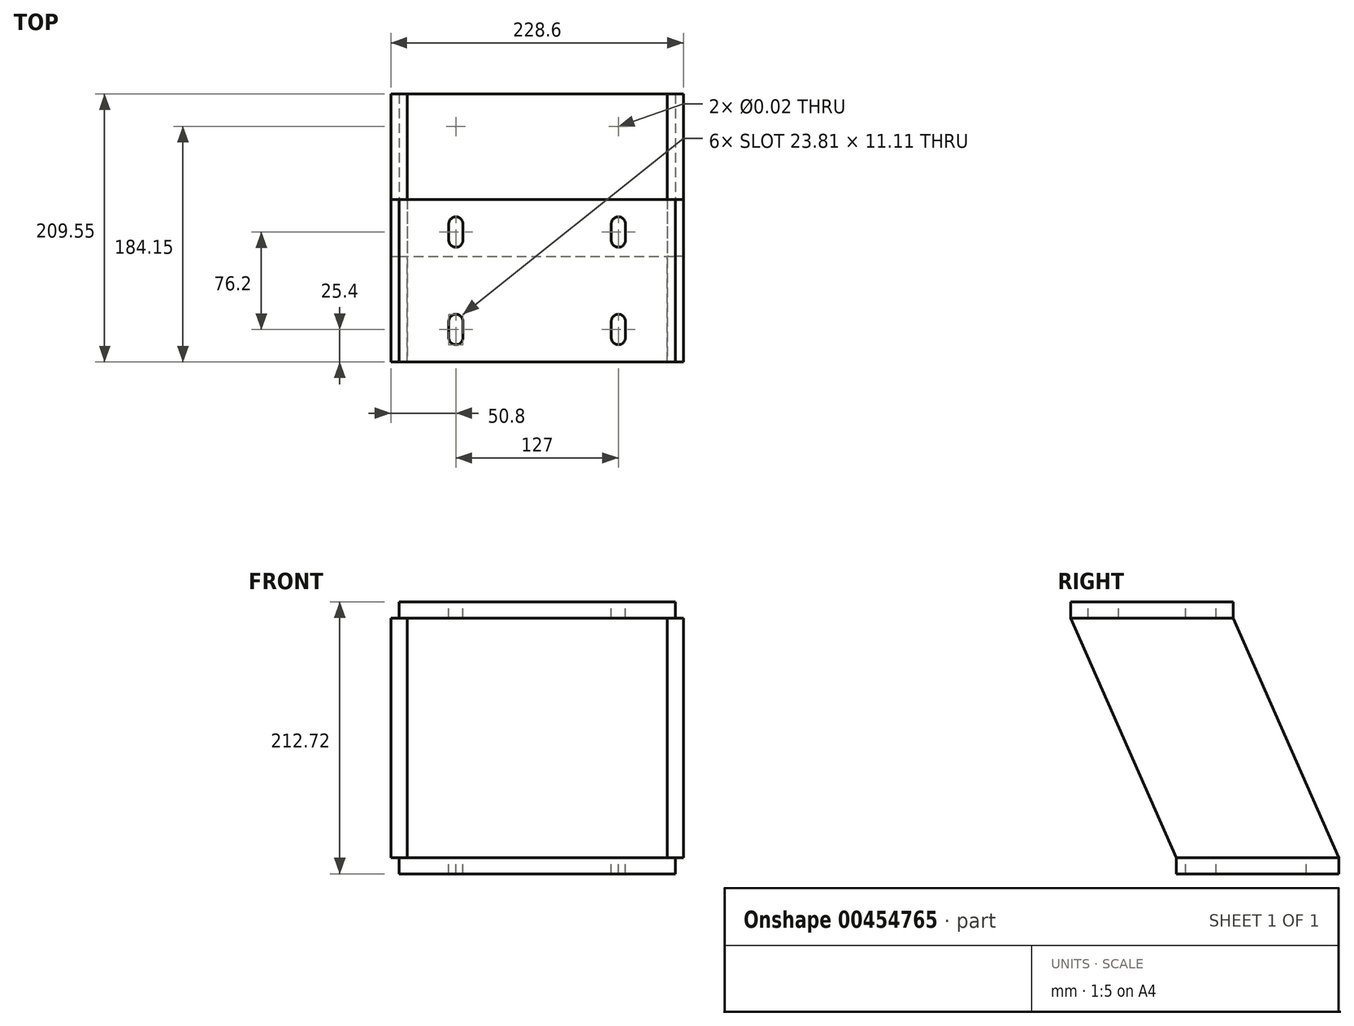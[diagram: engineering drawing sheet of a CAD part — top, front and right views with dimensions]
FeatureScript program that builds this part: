
annotation { "Feature Type Name" : "Feature", "Feature Type Description" : "" }
export const myFeature = defineFeature(function(context is Context, id is Id, definition is map)
    precondition{}
    {
        {
            var Q0;
            Q0=qCreatedBy(makeId("Top.planeOp"),FACE);
            var sketch = newSketch(context, id + "F0", { "sketchPlane" : qUnion([Q0])});
            skLineSegment(sketch, "E0.bottom", {"start": v(-107.95, 63.5) * mm, "end": v(107.95, 63.5) * mm});
            skLineSegment(sketch, "E0.top", {"start": v(-107.95, -63.5) * mm, "end": v(107.95, -63.5) * mm});
            skLineSegment(sketch, "E0.left", {"start": v(-107.95, 63.5) * mm, "end": v(-107.95, -63.5) * mm});
            skLineSegment(sketch, "E0.right", {"start": v(107.95, 63.5) * mm, "end": v(107.95, -63.5) * mm});
            skPoint(sketch, "E0.middle", {"position": v(0, 0) * mm});
            skSolve(sketch);
        }
        {
            var Q0;
            Q0=qSketchRegion(id+"F0",true);
            extrude(context, id + "F1", {"entities" : qUnion([Q0]), "depth" : 12.7 * mm});
        }
        {
            var Q0;
            Q0=makeQuery(id+"F1.opExtrude","CAP_FACE",FACE,{"disambiguationData":[OSD([sQuery(id+"F0.wireOp",EDGE,"E0.bottom"),sQuery(id+"F0.wireOp",EDGE,"E0.top"),sQuery(id+"F0.wireOp",EDGE,"E0.left"),sQuery(id+"F0.wireOp",EDGE,"E0.right")])],"isStart":false});
            var sketch = newSketch(context, id + "F2", { "sketchPlane" : qUnion([Q0])});
            skLineSegment(sketch, "E1.bottom", {"start": v(-63.5, 38.1) * mm, "end": v(63.5, 38.1) * mm, "construction": true});
            skLineSegment(sketch, "E1.top", {"start": v(-63.5, -38.1) * mm, "end": v(63.5, -38.1) * mm, "construction": true});
            skLineSegment(sketch, "E1.left", {"start": v(-63.5, 38.1) * mm, "end": v(-63.5, -38.1) * mm, "construction": true});
            skLineSegment(sketch, "E1.right", {"start": v(63.5, 38.1) * mm, "end": v(63.5, -38.1) * mm, "construction": true});
            skPoint(sketch, "E1.middle", {"position": v(0, 0) * mm});
            skPoint(sketch, "E2", {"position": v(-63.5, 38.1) * mm});
            skPoint(sketch, "E3", {"position": v(63.5, 38.1) * mm});
            skPoint(sketch, "E4", {"position": v(63.5, -38.1) * mm});
            skPoint(sketch, "E5", {"position": v(-63.5, -38.1) * mm});
            skSolve(sketch);
        }
        {
            var Q0;
            Q0=sQuery(id+"F2.wireOp",VERTEX,"E2");
            var Q1;
            Q1=sQuery(id+"F2.wireOp",VERTEX,"E3");
            var Q2;
            Q2=sQuery(id+"F2.wireOp",VERTEX,"E4");
            var Q3;
            Q3=sQuery(id+"F2.wireOp",VERTEX,"E5");
            var Q4;
            Q4=makeQuery(id+"F1.opExtrude","SWEPT_BODY",BODY,{"disambiguationData":[OSD([sQuery(id+"F0.wireOp",EDGE,"E0.bottom"),sQuery(id+"F0.wireOp",EDGE,"E0.top"),sQuery(id+"F0.wireOp",EDGE,"E0.left"),sQuery(id+"F0.wireOp",EDGE,"E0.right")])]});
            hole(context, id + "F3", {"style" : HoleStyle.SIMPLE, "endStyle" : HoleEndStyle.THROUGH, "standardTappedOrClearance" : lookupTablePath({ "standard" : "ANSI", "size" : "9/16 (0.56)", "type" : "Drilled" }), "standardBlindInLast" : lookupTablePath({ "standard" : "ANSI", "size" : "9/16", "type" : "Drilled" }), "holeDiameter" : 9 / 406.4 * mm, "locations" : qUnion([Q0, Q1, Q2, Q3]), "scope" : qUnion([Q4]), "isTappedThrough" : true});
        }
        {
            var Q0;
            Q0=qCreatedBy(makeId("Top.planeOp"),FACE);
            cPlane(context, id + "F4", {"entities" : qUnion([Q0]), "cplaneType" : CPlaneType.OFFSET, "offset" : 212.72 * mm, "width" : 152.4 * mm, "height" : 152.4 * mm});
        }
        {
            var Q0;
            Q0=qCreatedBy(id+"F4.planeOp",FACE);
            var sketch = newSketch(context, id + "F5", { "sketchPlane" : qUnion([Q0])});
            skLineSegment(sketch, "E6.0", {"start": v(-107.95, 63.5) * mm, "end": v(107.95, 63.5) * mm, "construction": true});
            skLineSegment(sketch, "E7.0", {"start": v(-107.95, -19.05) * mm, "end": v(107.95, -19.05) * mm, "construction": true});
            skLineSegment(sketch, "E8.bottom", {"start": v(-107.95, -19.05) * mm, "end": v(107.95, -19.05) * mm});
            skLineSegment(sketch, "E8.top", {"start": v(-107.95, -146.05) * mm, "end": v(107.95, -146.05) * mm});
            skLineSegment(sketch, "E8.left", {"start": v(-107.95, -19.05) * mm, "end": v(-107.95, -146.05) * mm});
            skLineSegment(sketch, "E8.right", {"start": v(107.95, -19.05) * mm, "end": v(107.95, -146.05) * mm});
            skSolve(sketch);
        }
        {
            var Q0;
            Q0=qSketchRegion(id+"F5",true);
            extrude(context, id + "F6", {"entities" : qUnion([Q0]), "oppositeDirection" : true, "depth" : 12.7 * mm});
        }
        {
            var Q0;
            Q0=makeQuery(id+"F6.opExtrude","CAP_FACE",FACE,{"disambiguationData":[OSD([sQuery(id+"F5.wireOp",EDGE,"E8.bottom"),sQuery(id+"F5.wireOp",EDGE,"E8.top"),sQuery(id+"F5.wireOp",EDGE,"E8.left"),sQuery(id+"F5.wireOp",EDGE,"E8.right")])],"isStart":true});
            var sketch = newSketch(context, id + "F7", { "sketchPlane" : qUnion([Q0])});
            skPoint(sketch, "E9.0", {"position": v(-107.95, -63.5) * mm});
            skLineSegment(sketch, "E10.0", {"start": v(-107.95, -19.05) * mm, "end": v(-107.95, -146.05) * mm, "construction": true});
            skLineSegment(sketch, "E11.0", {"start": v(107.95, -19.05) * mm, "end": v(107.95, -146.05) * mm, "construction": true});
            skLineSegment(sketch, "E12", {"start": v(-107.95, -19.05) * mm, "end": v(107.95, -146.05) * mm, "construction": true});
            skLineSegment(sketch, "E13", {"start": v(107.95, -19.05) * mm, "end": v(-107.95, -146.05) * mm, "construction": true});
            skLineSegment(sketch, "E14.bottom", {"start": v(-63.5, -44.45) * mm, "end": v(63.5, -44.45) * mm, "construction": true});
            skLineSegment(sketch, "E14.top", {"start": v(-63.5, -120.65) * mm, "end": v(63.5, -120.65) * mm, "construction": true});
            skLineSegment(sketch, "E14.left", {"start": v(-63.5, -44.45) * mm, "end": v(-63.5, -120.65) * mm, "construction": true});
            skLineSegment(sketch, "E14.right", {"start": v(63.5, -44.45) * mm, "end": v(63.5, -120.65) * mm, "construction": true});
            skPoint(sketch, "E14.middle", {"position": v(0, -82.55) * mm});
            skPoint(sketch, "E15", {"position": v(-63.5, -44.45) * mm});
            skPoint(sketch, "E16", {"position": v(63.5, -44.45) * mm});
            skPoint(sketch, "E17", {"position": v(63.5, -120.65) * mm});
            skPoint(sketch, "E18", {"position": v(-63.5, -120.65) * mm});
            skLineSegment(sketch, "E19", {"start": v(-63.5, -38.1) * mm, "end": v(-63.5, -50.8) * mm});
            skArc(sketch, "E20.0.startCap", {"start": v(-69.06, -38.1) * mm, "mid": v(-63.5, -32.54) * mm, "end": v(-57.94, -38.1) * mm});
            skArc(sketch, "E20.0.endCap", {"start": v(-57.94, -50.8) * mm, "mid": v(-63.5, -56.36) * mm, "end": v(-69.06, -50.8) * mm});
            skLineSegment(sketch, "E20.0.left", {"start": v(-57.94, -38.1) * mm, "end": v(-57.94, -50.8) * mm});
            skLineSegment(sketch, "E20.0.right", {"start": v(-69.06, -38.1) * mm, "end": v(-69.06, -50.8) * mm});
            skLineSegment(sketch, "E21.0.1.1", {"start": v(-63.5, -114.3) * mm, "end": v(-63.5, -127) * mm});
            skArc(sketch, "E21.0.1.2", {"start": v(-69.06, -114.3) * mm, "mid": v(-63.5, -108.74) * mm, "end": v(-57.94, -114.3) * mm});
            skArc(sketch, "E21.0.1.3", {"start": v(-57.94, -127) * mm, "mid": v(-63.5, -132.56) * mm, "end": v(-69.06, -127) * mm});
            skLineSegment(sketch, "E21.0.1.4", {"start": v(-57.94, -114.3) * mm, "end": v(-57.94, -127) * mm});
            skLineSegment(sketch, "E21.0.1.5", {"start": v(-69.06, -114.3) * mm, "end": v(-69.06, -127) * mm});
            skLineSegment(sketch, "E21.1.0.1", {"start": v(63.5, -38.1) * mm, "end": v(63.5, -50.8) * mm});
            skArc(sketch, "E21.1.0.2", {"start": v(57.94, -38.1) * mm, "mid": v(63.5, -32.54) * mm, "end": v(69.06, -38.1) * mm});
            skArc(sketch, "E21.1.0.3", {"start": v(69.06, -50.8) * mm, "mid": v(63.5, -56.36) * mm, "end": v(57.94, -50.8) * mm});
            skLineSegment(sketch, "E21.1.0.4", {"start": v(69.06, -38.1) * mm, "end": v(69.06, -50.8) * mm});
            skLineSegment(sketch, "E21.1.0.5", {"start": v(57.94, -38.1) * mm, "end": v(57.94, -50.8) * mm});
            skLineSegment(sketch, "E21.1.1.1", {"start": v(63.5, -114.3) * mm, "end": v(63.5, -127) * mm});
            skArc(sketch, "E21.1.1.2", {"start": v(57.94, -114.3) * mm, "mid": v(63.5, -108.74) * mm, "end": v(69.06, -114.3) * mm});
            skArc(sketch, "E21.1.1.3", {"start": v(69.06, -127) * mm, "mid": v(63.5, -132.56) * mm, "end": v(57.94, -127) * mm});
            skLineSegment(sketch, "E21.1.1.4", {"start": v(69.06, -114.3) * mm, "end": v(69.06, -127) * mm});
            skLineSegment(sketch, "E21.1.1.5", {"start": v(57.94, -114.3) * mm, "end": v(57.94, -127) * mm});
            skLineSegment(sketch, "E21.direction1", {"start": v(-69.06, -50.8) * mm, "end": v(57.94, -50.8) * mm, "construction": true});
            skLineSegment(sketch, "E21.direction2", {"start": v(-69.06, -50.8) * mm, "end": v(-69.06, -127) * mm, "construction": true});
            skSolve(sketch);
        }
        {
            var Q0;
            Q0=qSketchRegion(id+"F7",true);
            extrude(context, id + "F8", {"entities" : qUnion([Q0]), "operationType" : NewBodyOperationType.REMOVE, "endBound" : BoundingType.THROUGH_ALL, "oppositeDirection" : true, "depth" : 25.4 * mm});
        }
        {
            var Q0;
            Q0=makeQuery(id+"F6.opExtrude","SWEPT_FACE",FACE,{"disambiguationData":[OSD([sQuery(id+"F5.wireOp",EDGE,"E8.right")])]});
            var sketch = newSketch(context, id + "F9", { "sketchPlane" : qUnion([Q0])});
            skLineSegment(sketch, "E22.0", {"start": v(-19.05, 200.03) * mm, "end": v(-146.05, 200.03) * mm});
            skLineSegment(sketch, "E23.0", {"start": v(63.5, 12.7) * mm, "end": v(-63.5, 12.7) * mm});
            skLineSegment(sketch, "E24", {"start": v(-146.05, 200.02) * mm, "end": v(-63.5, 12.7) * mm});
            skLineSegment(sketch, "E25", {"start": v(-19.05, 200.03) * mm, "end": v(63.5, 12.7) * mm});
            skSolve(sketch);
        }
        {
            var Q0;
            Q0=qSketchRegion(id+"F9",true);
            extrude(context, id + "F10", {"entities" : qUnion([Q0]), "endBound" : BoundingType.SYMMETRIC, "depth" : 12.7 * mm});
        }
        {
            var Q0;
            Q0=makeQuery(id+"F10.opExtrude","SWEPT_BODY",BODY,{"disambiguationData":[OSD([sQuery(id+"F9.wireOp",EDGE,"E22.0"),sQuery(id+"F9.wireOp",EDGE,"E23.0"),sQuery(id+"F9.wireOp",EDGE,"E24"),sQuery(id+"F9.wireOp",EDGE,"E25")])]});
            var Q1;
            Q1=qCreatedBy(makeId("Right.planeOp"),FACE);
            mirror(context, id + "F11", {"entities" : qUnion([Q0]), "mirrorPlane" : qUnion([Q1])});
        }
    });
